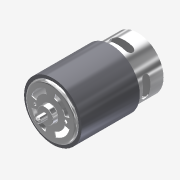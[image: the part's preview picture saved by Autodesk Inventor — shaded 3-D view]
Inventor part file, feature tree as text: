
AUTODESK INVENTOR PART (.ipt)
format: ipt  version: 2013 (Build 170138000, 138)  size: 359,936 bytes
history: native  units: mm (DEFAULTED — no unit token found)
features: sketch x15, extrude x13, fillet x3, pattern_circular x3, plane x3, hole x2, mirror x2, shell x1, chamfer x1
ambient origin geometry x8: Origin, YZ Plane, XZ Plane, XY Plane, X Axis, Y Axis, Z Axis, Center Point
bodies: Solid1 (feature_tree)
feature tree (43):
  extrude  "Extrusion1"  Depth=71.3mm TaperAngle=0.0deg
  fillet  "Fillet1"  Radius=2.0mm
  shell  "Shell1"  Thickness=0.62mm
  extrude  "Extrusion2"  Depth=4.5mm TaperAngle=0.0deg
  fillet  "Fillet2"  Radius=0.5mm
  extrude  "Extrusion3"  Depth=7.6mm TaperAngle=0.0deg
  fillet  "Fillet3"  Radius=2.5mm
  hole  "Hole1"  [1 undecoded]
  mirror  "Mirror1"
  extrude  "Extrusion4"  Depth=16.0mm
  pattern_circular  "Circular Pattern1"  Count=4 Angle=360.0deg
  plane  "Work Plane1"
  extrude  "Extrusion5"  Depth=0.62mm TaperAngle=0.0deg
  extrude  "Extrusion6"  Depth=0.62mm TaperAngle=0.0deg
  extrude  "Extrusion7"  Depth=3.0mm TaperAngle=0.0deg
  extrude  "Extrusion8"  Depth=0.8mm TaperAngle=0.0deg
  extrude  "Extrusion9"  Depth=1.0mm TaperAngle=0.0deg
  extrude  "Extrusion10"  Depth=3.15mm
  pattern_circular  "Circular Pattern2"  [2 undecoded]
  extrude  "Extrusion11"  Depth=1.0mm TaperAngle=0.0deg
  chamfer  "Chamfer1"  Distance=40.0mm Angle=360.0deg
  hole  "Hole2"  [1 undecoded]
  mirror  "Mirror2"
  plane  "Work Plane2"
  extrude  "Extrusion12"  Depth=3.8mm
  plane  "Work Plane3"
  extrude  "Flux Ring"  Depth=14.0mm
  pattern_circular  "Circular Pattern3"  [2 undecoded]
  sketch  "Sketch1"  dims[d0=42.1mm d1=71.3mm d2=0.0mm d3=2.0mm d4=0.62mm]
  sketch  "Sketch2"  dims[d5=13.0mm d6=4.5mm d7=0.0mm d8=0.5mm]
  sketch  "Sketch3"  dims[d9=5.0mm d10=7.6mm d11=0.0mm d12=2.5mm]
  sketch  "Sketch4"  dims[d13=12.5mm]
  sketch  "Sketch5"  dims[d14=2.5mm d15=6.0mm d16=4.0mm d17=2.0mm d18=14.3117mm d19=8.0mm d20=20.594885mm d21=15.0deg]
  sketch  "Sketch6"  dims[d22=15.0deg d23=16.0mm]
  sketch  "Sketch7"  dims[d24=12.0mm]
  sketch  "Sketch8"  dims[d25=10.0mm d26=0.0mm d27=40.0mm d29=360.0deg]
  sketch  "Sketch9"  dims[d30=-1.75mm d31=0.62mm d32=0.0mm]
  sketch  "Sketch10"  dims[d33=24.0mm d34=0.62mm d35=0.0mm]
  sketch  "Sketch11"  dims[d36=10.75mm d37=3.0mm d38=0.0mm]
  sketch  "Sketch12"  dims[d39=6.9mm d40=0.8mm d41=0.0mm]
  sketch  "Sketch13"  dims[d42=3.2mm d43=1.0mm d44=0.0mm]
  sketch  "Sketch14"  dims[d45=3.15mm d46=3.15mm]
  sketch  "Sketch15"  dims[d47=9.875mm d48=6.5mm d49=1.0mm d50=0.0mm d51=40.0mm d53=360.0deg d54=0.5mm d55=3.8mm d56=14.0mm d57=7.2mm d58=0.0mm d59=1.0mm d60=2.0mm d61=3.0mm d62=2.0mm d63=6.0mm d64=4.0mm d65=2.0mm d66=14.3117mm d67=1.0mm d68=20.594885mm d69=18.0mm d70=10.75mm d71=5.9mm d72=12.0mm d73=7.2mm d74=0.0mm d75=45.0deg d76=2.45mm d77=47.5mm d78=0.0mm d79=40.0mm d80=360.0deg]
note: 6 required parameter values undecoded (feature->parameter linkage not recoverable at this tier; creation-order binding heuristic only, values carry confidence <= 0.55)
